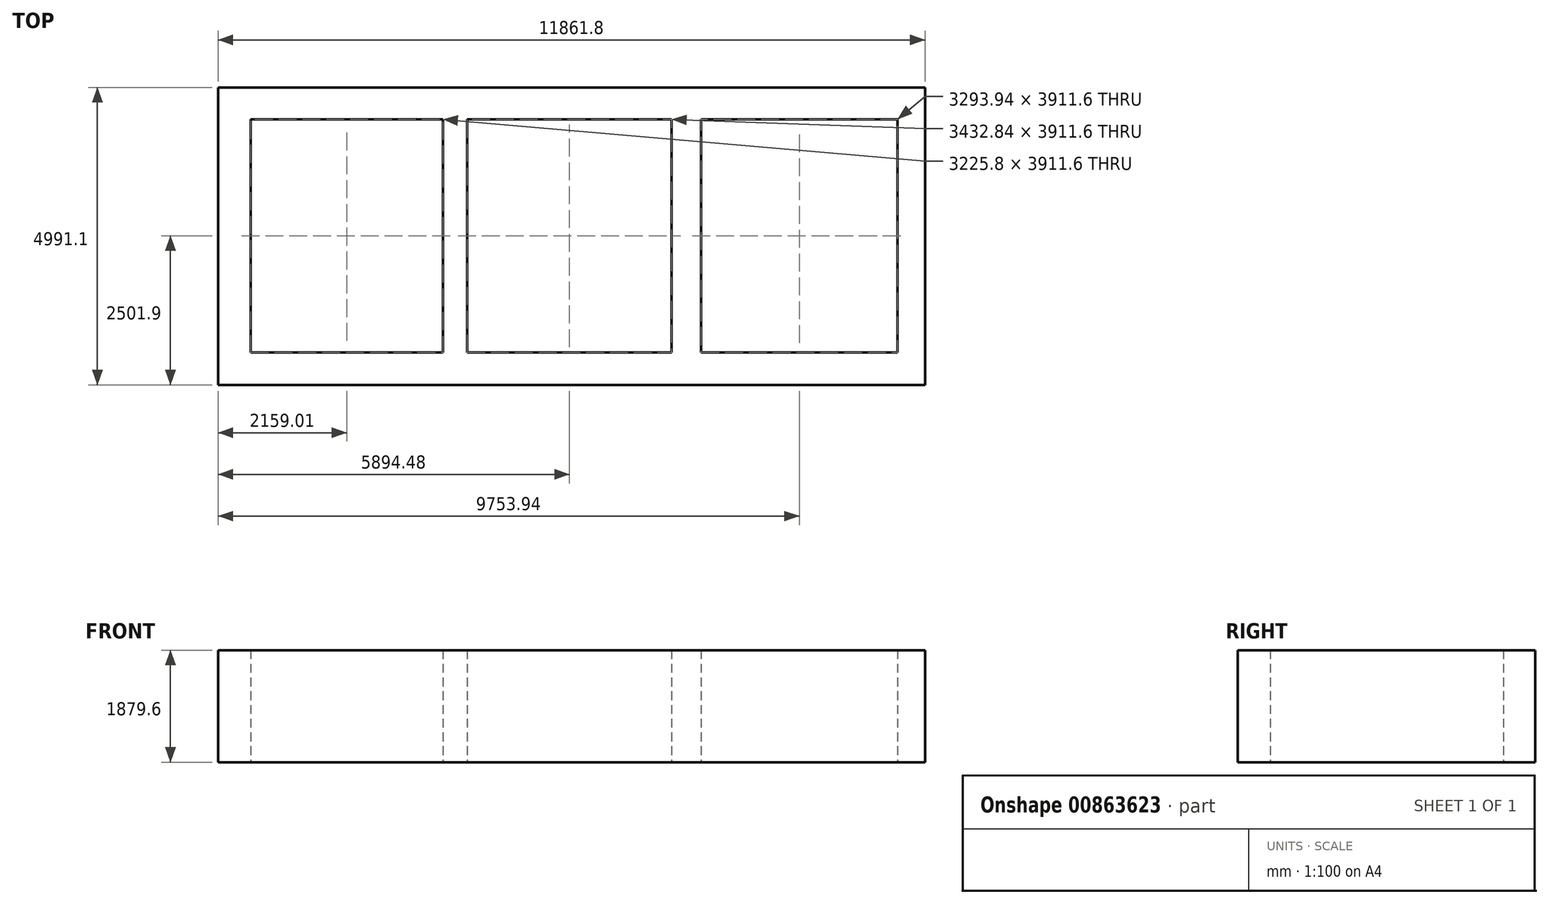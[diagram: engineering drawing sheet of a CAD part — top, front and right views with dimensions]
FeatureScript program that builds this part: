
annotation { "Feature Type Name" : "Feature", "Feature Type Description" : "" }
export const myFeature = defineFeature(function(context is Context, id is Id, definition is map)
    precondition{}
    {
        {
            var Q0;
            Q0=qCreatedBy(makeId("Top.planeOp"),FACE);
            var sketch = newSketch(context, id + "F0", { "sketchPlane" : qUnion([Q0])});
            skLineSegment(sketch, "E0.bottom", {"start": v(-2331.62, 3890.6) * mm, "end": v(9530.18, 3890.6) * mm});
            skLineSegment(sketch, "E0.top", {"start": v(-2331.62, -1100.5) * mm, "end": v(9530.18, -1100.5) * mm});
            skLineSegment(sketch, "E0.left", {"start": v(-2331.62, 3890.6) * mm, "end": v(-2331.62, -1100.5) * mm});
            skLineSegment(sketch, "E0.right", {"start": v(9530.18, 3890.6) * mm, "end": v(9530.18, -1100.5) * mm});
            skLineSegment(sketch, "E1.bottom", {"start": v(-1785.52, 3357.2) * mm, "end": v(1440.28, 3357.2) * mm});
            skLineSegment(sketch, "E1.top", {"start": v(-1785.52, -554.4) * mm, "end": v(1440.28, -554.4) * mm});
            skLineSegment(sketch, "E1.left", {"start": v(-1785.52, 3357.2) * mm, "end": v(-1785.52, -554.4) * mm});
            skLineSegment(sketch, "E1.right", {"start": v(1440.28, 3357.2) * mm, "end": v(1440.28, -554.4) * mm});
            skLineSegment(sketch, "E2.bottom", {"start": v(1846.44, 3357.2) * mm, "end": v(5279.28, 3357.2) * mm});
            skLineSegment(sketch, "E2.top", {"start": v(1846.44, -554.4) * mm, "end": v(5279.28, -554.4) * mm});
            skLineSegment(sketch, "E2.left", {"start": v(1846.44, 3357.2) * mm, "end": v(1846.44, -554.4) * mm});
            skLineSegment(sketch, "E2.right", {"start": v(5279.28, 3357.2) * mm, "end": v(5279.28, -554.4) * mm});
            skLineSegment(sketch, "E3.bottom", {"start": v(5775.35, 3357.2) * mm, "end": v(9069.29, 3357.2) * mm});
            skLineSegment(sketch, "E3.top", {"start": v(5775.35, -554.4) * mm, "end": v(9069.29, -554.4) * mm});
            skLineSegment(sketch, "E3.left", {"start": v(5775.35, 3357.2) * mm, "end": v(5775.35, -554.4) * mm});
            skLineSegment(sketch, "E3.right", {"start": v(9069.29, 3357.2) * mm, "end": v(9069.29, -554.4) * mm});
            skSolve(sketch);
        }
        {
            var Q0;
            Q0 = qSketchRegion(id + "F0", true);
            extrude(context, id + "F1", {"entities" : qUnion([Q0]), "depth" : 1879.6 * mm, "offsetDistance" : 25.4 * mm});
        }
        {
            var Q0;
            Q0=sQuery(id+"F0.wireOp",EDGE,"E1.top");
            var Q1;
            Q1=sQuery(id+"F0.wireOp",EDGE,"E1.bottom");
            var Q2;
            Q2=sQuery(id+"F0.wireOp",EDGE,"E1.right");
            var Q3;
            Q3=sQuery(id+"F0.wireOp",EDGE,"E1.left");
            extrude(context, id + "F2", {"bodyType" : ToolBodyType.SURFACE, "surfaceEntities" : qUnion([Q0, Q1, Q2, Q3]), "depth" : 2540 * mm, "offsetDistance" : 25.4 * mm});
        }
    });
